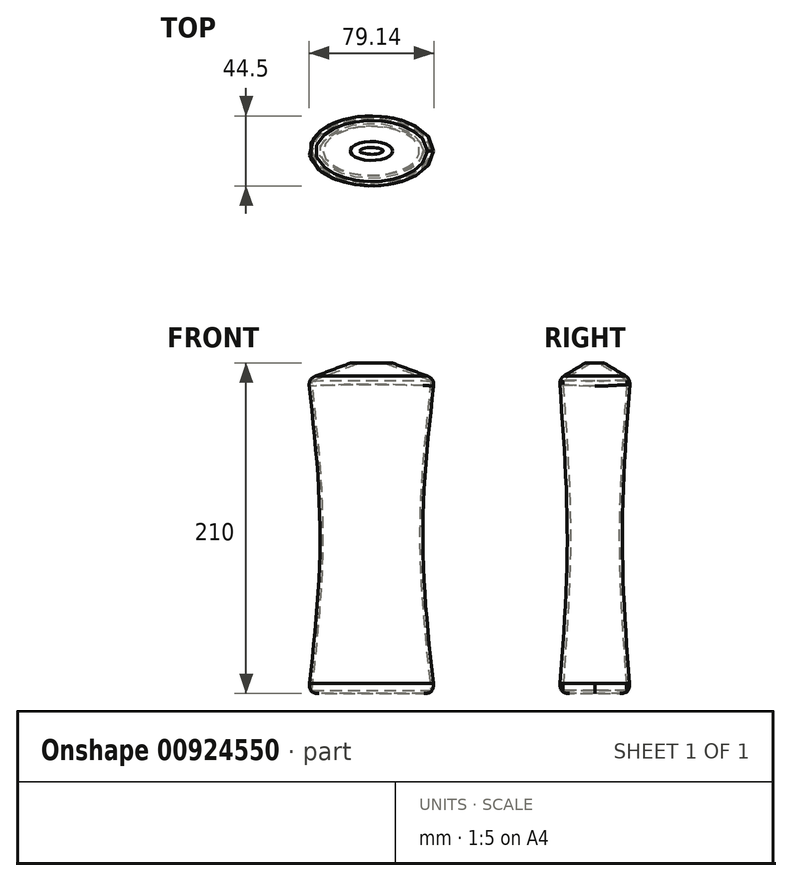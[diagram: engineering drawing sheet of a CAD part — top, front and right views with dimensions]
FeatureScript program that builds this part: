
annotation { "Feature Type Name" : "Feature", "Feature Type Description" : "" }
export const myFeature = defineFeature(function(context is Context, id is Id, definition is map)
    precondition{}
    {
        {
            var Q0;
            Q0=qCreatedBy(makeId("Top.planeOp"),FACE);
            var sketch = newSketch(context, id + "F0", { "sketchPlane" : qUnion([Q0])});
            skEllipse(sketch, "E0", {"center": v(0, 0) * mm, "majorRadius": 40 * mm, "minorRadius": 22.5 * mm, "majorAxis": v(1, 0)});
            skSolve(sketch);
        }
        {
            var Q0;
            Q0=qCreatedBy(makeId("Top.planeOp"),FACE);
            cPlane(context, id + "F1", {"entities" : qUnion([Q0]), "cplaneType" : CPlaneType.OFFSET, "offset" : 100 * mm, "width" : 150 * mm, "height" : 150 * mm});
        }
        {
            var Q0;
            Q0=qCreatedBy(id+"F1.planeOp",FACE);
            var sketch = newSketch(context, id + "F2", { "sketchPlane" : qUnion([Q0])});
            skEllipse(sketch, "E1", {"center": v(0, 0) * mm, "majorRadius": 32.64 * mm, "minorRadius": 17.5 * mm, "majorAxis": v(1, 0)});
            skSolve(sketch);
        }
        {
            var Q0;
            Q0=qCreatedBy(id+"F1.planeOp",FACE);
            cPlane(context, id + "F3", {"entities" : qUnion([Q0]), "cplaneType" : CPlaneType.OFFSET, "offset" : 100 * mm, "width" : 150 * mm, "height" : 150 * mm});
        }
        {
            var Q0;
            Q0=qCreatedBy(id+"F3.planeOp",FACE);
            var sketch = newSketch(context, id + "F4", { "sketchPlane" : qUnion([Q0])});
            skEllipse(sketch, "E2.0", {"center": v(0, 0) * mm, "majorRadius": 40 * mm, "minorRadius": 22.5 * mm, "majorAxis": v(1, 0)});
            skSolve(sketch);
        }
        {
            var Q0;
            Q0=makeQuery(id+"F0.imprint","IMPRINT",FACE,{"disambiguationData":[TD([[makeQuery(id+"F0.imprint","IMPRINT",EDGE,{"derivedFrom":sQuery(id+"F0.wireOp",EDGE,"E0")}),1.0]])]});
            var Q1;
            Q1=makeQuery(id+"F2.imprint","IMPRINT",FACE,{"disambiguationData":[TD([[makeQuery(id+"F2.imprint","IMPRINT",EDGE,{"derivedFrom":sQuery(id+"F2.wireOp",EDGE,"E1")}),1.0]])]});
            var Q2;
            Q2=makeQuery(id+"F4.imprint","IMPRINT",FACE,{"disambiguationData":[TD([[makeQuery(id+"F4.imprint","IMPRINT",EDGE,{"derivedFrom":sQuery(id+"F4.wireOp",EDGE,"E2.0")}),1.0]])]});
            loft(context, id + "F5", {"sheetProfilesArray" : [{ "sheetProfileEntities" : qUnion([Q0]) }, { "sheetProfileEntities" : qUnion([Q1]) }, { "sheetProfileEntities" : qUnion([Q2]) }]});
        }
        {
            var Q0;
            Q0=qCreatedBy(id+"F3.planeOp",FACE);
            cPlane(context, id + "F6", {"entities" : qUnion([Q0]), "cplaneType" : CPlaneType.OFFSET, "offset" : 10 * mm, "width" : 150 * mm, "height" : 150 * mm});
        }
        {
            var Q0;
            Q0=qCreatedBy(id+"F6.planeOp",FACE);
            var sketch = newSketch(context, id + "F7", { "sketchPlane" : qUnion([Q0])});
            skEllipse(sketch, "E3", {"center": v(0, 0) * mm, "majorRadius": 13.4 * mm, "minorRadius": 6.04 * mm, "majorAxis": v(1, 0)});
            skSolve(sketch);
        }
        {
            var Q1;
            Q1=makeQuery(id+"F5.opLoft","CAP_FACE",FACE,{"disambiguationData":[OSD([makeQuery(id+"F4.imprint","IMPRINT",FACE,{"disambiguationData":[TD([[makeQuery(id+"F4.imprint","IMPRINT",EDGE,{"derivedFrom":sQuery(id+"F4.wireOp",EDGE,"E2.0")}),1.0]])]})])],"isStart":true});
            var Q2;
            Q2=makeQuery(id+"F7.imprint","IMPRINT",FACE,{"disambiguationData":[TD([[makeQuery(id+"F7.imprint","IMPRINT",EDGE,{"derivedFrom":sQuery(id+"F7.wireOp",EDGE,"E3")}),1.0]])]});
            loft(context, id + "F8", {"operationType" : NewBodyOperationType.ADD, "sheetProfilesArray" : [{ "sheetProfileEntities" : qUnion([Q1]) }, { "sheetProfileEntities" : qUnion([Q2]) }]});
        }
        {
            var Q0;
            Q0=makeQuery(id+"F8.opLoft","CAP_FACE",FACE,{"disambiguationData":[OSD([makeQuery(id+"F7.imprint","IMPRINT",FACE,{"disambiguationData":[TD([[makeQuery(id+"F7.imprint","IMPRINT",EDGE,{"derivedFrom":sQuery(id+"F7.wireOp",EDGE,"E3")}),1.0]])]})])],"isStart":true});
            shell(context, id + "F9", {"entities" : qUnion([Q0]), "thickness" : 2 * mm});
        }
        {
            var Q0;
            {var subQ0=sQuery(id+"F4.wireOp",EDGE,"E2.0");Q0=makeQuery(id+"F8.boolean.opBoolean","MERGE",EDGE,{"derivedFrom":[makeQuery(id+"F5.opLoft","MID_CAP_EDGE",EDGE,{"disambiguationData":[OSD([subQ0])],"capPos":2.0}),makeQuery(id+"F8.opLoft","MID_CAP_EDGE",EDGE,{"disambiguationData":[OSD([subQ0])],"capPos":0.0})]});}
            var Q1;
            Q1=makeQuery(id+"F5.opLoft","MID_CAP_EDGE",EDGE,{"disambiguationData":[OSD([sQuery(id+"F0.wireOp",EDGE,"E0")])],"capPos":0.0});
            fillet(context, id + "F10", {"entities" : qUnion([Q0, Q1]), "radius" : 6 * mm, "rho" : 0.5, "crossSection" : FilletCrossSection.CONIC, "allowEdgeOverflow" : false});
        }
    });
